# Revit family: Vaportite - Ceiling(VTC) 100w MB 16w LED
name_source: partatom
category: Lighting Fixtures
units: mm (PartAtom-declared; Revit-internal decimal feet)

## family parameters
Always vertical = Yes
Cut with Voids When Loaded = No
Light Source = Yes
OmniClass Number = 23.80.70.00
OmniClass Title = Lighting
Part Type = Normal
Room Calculation Point = No
Round Connector Dimension = Use Diameter
Shared = No
Work Plane-Based = No

## types (1)
- VTC100GL
    Apparent Load = 16 VA
    Body Colour = Cast aluminium
    Body Material = body
    Bulb = Bulb
    CRI = >90
    Color Filter = 16777215
    Construction Material = Cast aluminum.
    Default Elevation = 0' - 0"
    Description = 120-277 Voltage
    Dimming = 1%
    Dimming Lamp Color Temperature Shift = <None>
    Efficiency = 65-125 lumens per watt
    Fixture Diameter = 0' - 6"
    Fixture Height = 0' - 10"
    HUB = Texture Black
    INSIDE BODY = INSIDE BODY
    Lamp = LED
    Life = L70 50,000 hours
    Load Classification = Lighting
    Manufacturer = ANP Lighting
    Model = VTC100GL
    Photometric Web File = generic.ies
    Power Factor = 1
    Tilt Angle = 90.00°
    URL = https://www.anplighting.com
    VTC100GL = Yes
    Voltage = 277 V
    Warranty = 5 year limited warranty
    Wattage Comments = 16W
    Weight = 4 lbs

## geometry (parser evidence)
native form markers: Sweep x7
no freeform markers — native parametric forms only
